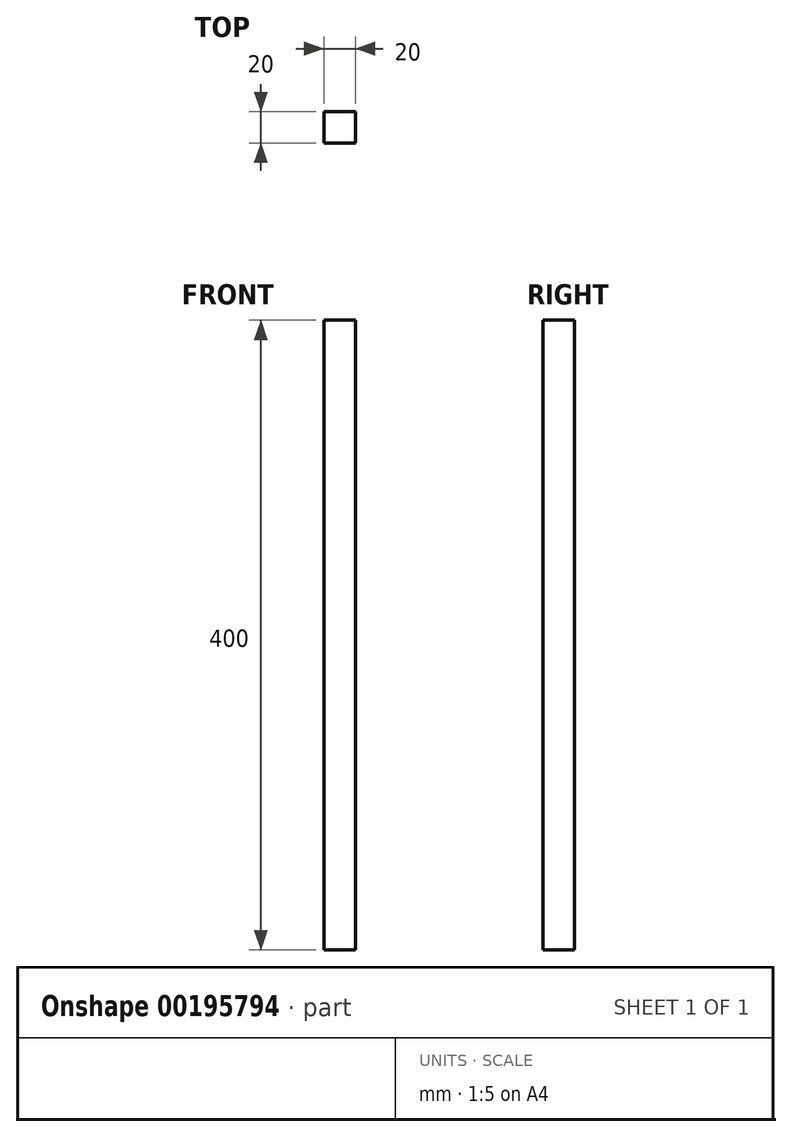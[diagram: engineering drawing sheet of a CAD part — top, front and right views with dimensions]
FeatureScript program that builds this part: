
annotation { "Feature Type Name" : "Feature", "Feature Type Description" : "" }
export const myFeature = defineFeature(function(context is Context, id is Id, definition is map)
    precondition{}
    {
        {
            var Q0;
            Q0=qCreatedBy(makeId("Top.planeOp"),FACE);
            var sketch = newSketch(context, id + "F0", { "sketchPlane" : qUnion([Q0])});
            skLineSegment(sketch, "E0.bottom", {"start": v(-96.07, -23.85) * mm, "end": v(-76.07, -23.85) * mm});
            skLineSegment(sketch, "E0.top", {"start": v(-96.07, -3.85) * mm, "end": v(-76.07, -3.85) * mm});
            skLineSegment(sketch, "E0.left", {"start": v(-96.07, -23.85) * mm, "end": v(-96.07, -3.85) * mm});
            skLineSegment(sketch, "E0.right", {"start": v(-76.07, -23.85) * mm, "end": v(-76.07, -3.85) * mm});
            skSolve(sketch);
        }
        {
            var Q0;
            Q0=makeQuery(id+"F0.imprint","IMPRINT",FACE,{"disambiguationData":[TD([[makeQuery(id+"F0.imprint","IMPRINT",EDGE,{"derivedFrom":sQuery(id+"F0.wireOp",EDGE,"E0.bottom")}),1.0]])]});
            extrude(context, id + "F1", {"entities" : qUnion([Q0]), "depth" : 400 * mm});
        }
    });
